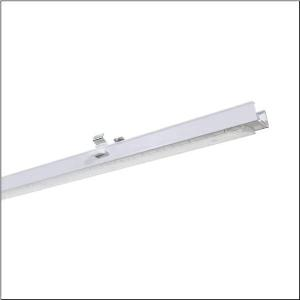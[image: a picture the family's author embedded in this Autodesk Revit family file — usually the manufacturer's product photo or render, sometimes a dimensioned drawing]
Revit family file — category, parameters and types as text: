
# Revit family: trunking_flex_31_51re11db49b
name_source: partatom
category: Lighting Fixtures
units: mm (PartAtom-declared; Revit-internal decimal feet)

## family parameters
Cut with Voids When Loaded = No
Host = Face
Light Source = No
Part Type = Normal
Room Calculation Point = No
Round Connector Dimension = Use Diameter
Shared = No

## types (1)
- --- (1 x LED, 8900 lm, 56 W, 4000K)
    Apparent Load = 56 VA
    CIE Flux Codes = 83 93 98 100 100
    Color Rendering = 80
    Color Temperature = 4000K
    Default Elevation = 1800 mm
    Description = Trunking Flex 31, luminaire insert, of extruded aluminium section, coated, traffic white (RAL 9016), length: 1.472mm, width: 91mm, height: 53mm, LED rated luminous flux: 8.900lm, light colour: 840, control gear: DALI 2, with system connector: socket, mains connection: 220..240V, AC, 50/60Hz, rated input power: 56W, primary light control with lens, of plastic, primary optical cover: cover, of PMMA, light emission: direct distribution, protection rating (complete): IP20, insulation class (complete): insulation class I (protective earthing), certification: CE, UKCA, impact resistance: IK02, permissible ambient temperature for indoor applications: -20..+40°C, packaging unit: 1 piece
    Height = 58 mm
    Lamp = 1 x LED
    Lamp Light Flux = 8900 lm
    Lamp Power = 56 W
    Lamp count = 1
    Length = 1472 mm
    Luminous efficacy = 159 lm/W
    Manufacturer = Siteco
    ModVariant = No
    Model = 51RE11DB49B
    Mounting Place = Ceiling
    Mounting Type = Pendant
    Number of Poles = 1
    OnlyDefault = Yes
    Power Factor = 1
    Product Name = Trunking Flex 31
    Product group = luminaire insert
    ProductGroupID = 901
    Protection Class = Protection class I
    Protection Degree = IP 20
    RLX_Detail_Level = 1
    RLX_Emergency_Light_Flux = 0 lm
    RLX_Emergency_Type = 0
    RLX_Emergency_Type_DB = No
    RlxData = <blob elided: 21685 chars, md5=7be02236>
    Socket = socket
    Standby Power = 0 W
    System Light Flux = 8900 lm
    System Power = 56 W
    Type Comments = individual setting: luminous flux: 100 % | (OFF | ON | OFF | OFF) | 1200 mA
    Type Image = l_1266702.jpg
    URL = http://relux.com
    VarID = @adj_001425
    Voltage = 0 V
    Weight = 0.00 kg
    Width = 65 mm

## geometry (parser evidence)
native form markers: Blend x4, Sweep x10
no freeform markers — native parametric forms only
